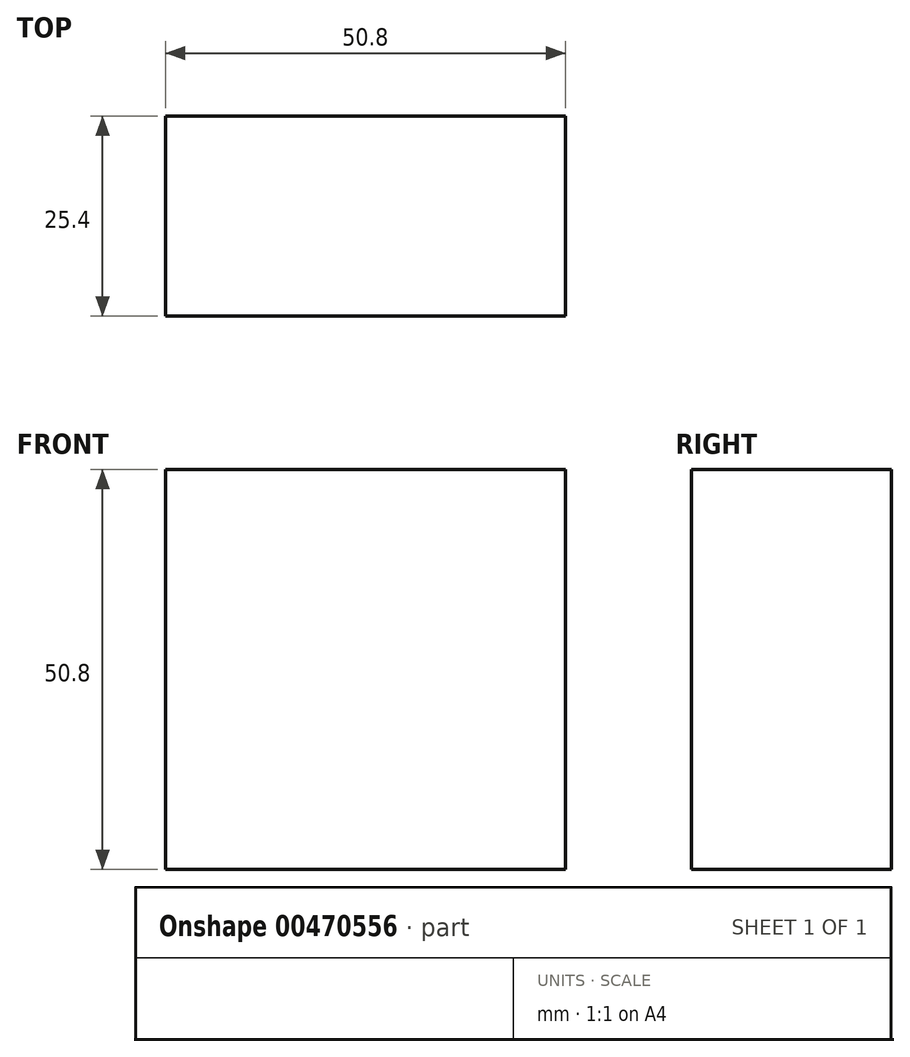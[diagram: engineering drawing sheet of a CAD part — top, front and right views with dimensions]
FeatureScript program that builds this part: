
annotation { "Feature Type Name" : "Feature", "Feature Type Description" : "" }
export const myFeature = defineFeature(function(context is Context, id is Id, definition is map)
    precondition{}
    {
        {
            var Q0;
            Q0=qCreatedBy(makeId("Front.planeOp"),FACE);
            var sketch = newSketch(context, id + "F0", { "sketchPlane" : qUnion([Q0])});
            skLineSegment(sketch, "E0.bottom", {"start": v(25.4, 25.4) * mm, "end": v(-25.4, 25.4) * mm});
            skLineSegment(sketch, "E0.top", {"start": v(25.4, -25.4) * mm, "end": v(-25.4, -25.4) * mm});
            skLineSegment(sketch, "E0.left", {"start": v(25.4, 25.4) * mm, "end": v(25.4, -25.4) * mm});
            skLineSegment(sketch, "E0.right", {"start": v(-25.4, 25.4) * mm, "end": v(-25.4, -25.4) * mm});
            skPoint(sketch, "E0.middle", {"position": v(0, 0) * mm});
            skSolve(sketch);
        }
        {
            var Q0;
            Q0=makeQuery(id+"F0.imprint","IMPRINT",FACE,{"disambiguationData":[TD([[makeQuery(id+"F0.imprint","IMPRINT",EDGE,{"derivedFrom":sQuery(id+"F0.wireOp",EDGE,"E0.bottom")}),1.0]])]});
            extrude(context, id + "F1", {"entities" : qUnion([Q0]), "depth" : 25.4 * mm});
        }
    });
